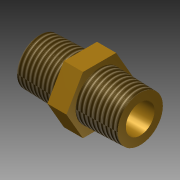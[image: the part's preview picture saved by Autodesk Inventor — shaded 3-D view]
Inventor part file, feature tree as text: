
AUTODESK INVENTOR PART (.ipt)
format: ipt  version: 2011 (Build 150239000, 239)  size: 104,960 bytes
history: native  units: mm (DEFAULTED — no unit token found)
features: thread x4, sketch x1, imported_body x1
ambient origin geometry x8: Origin, YZ Plane, XZ Plane, XY Plane, X Axis, Y Axis, Z Axis, Center Point
bodies: Solid1 (feature_tree)
feature tree (6):
  sketch  "Sketch1"
  imported_body  "Base1"
  thread  "Thread1"  [1 undecoded]
  thread  "Thread2"  [1 undecoded]
  thread  "Thread3"  [1 undecoded]
  thread  "Thread4"  [1 undecoded]
note: 4 required parameter values undecoded (feature->parameter linkage not recoverable at this tier; creation-order binding heuristic only, values carry confidence <= 0.55)
